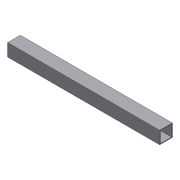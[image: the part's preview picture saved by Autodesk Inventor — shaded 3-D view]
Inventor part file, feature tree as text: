
AUTODESK INVENTOR PART (.ipt)
format: ipt  version: 2012 (Build 160160000, 160)  size: 72,704 bytes
history: native  units: in
note: dims shown in document units (in); Inventor stores cm internally (conversion verified against a paired STEP export)
features: extrude x1, shell x1, sketch x1
ambient origin geometry x8: Origin, YZ Plane, XZ Plane, XY Plane, X Axis, Y Axis, Z Axis, Center Point
bodies: Solid1 (feature_tree)
feature tree (3):
  extrude  "Extrusion1"  Depth=1.0in
  shell  "Shell2"  Thickness=12.0in
  sketch  "Sketch1"  dims[d2=1.0in d3=0.0in d5=1.0in d6=12.0in d8=0.0625in]
